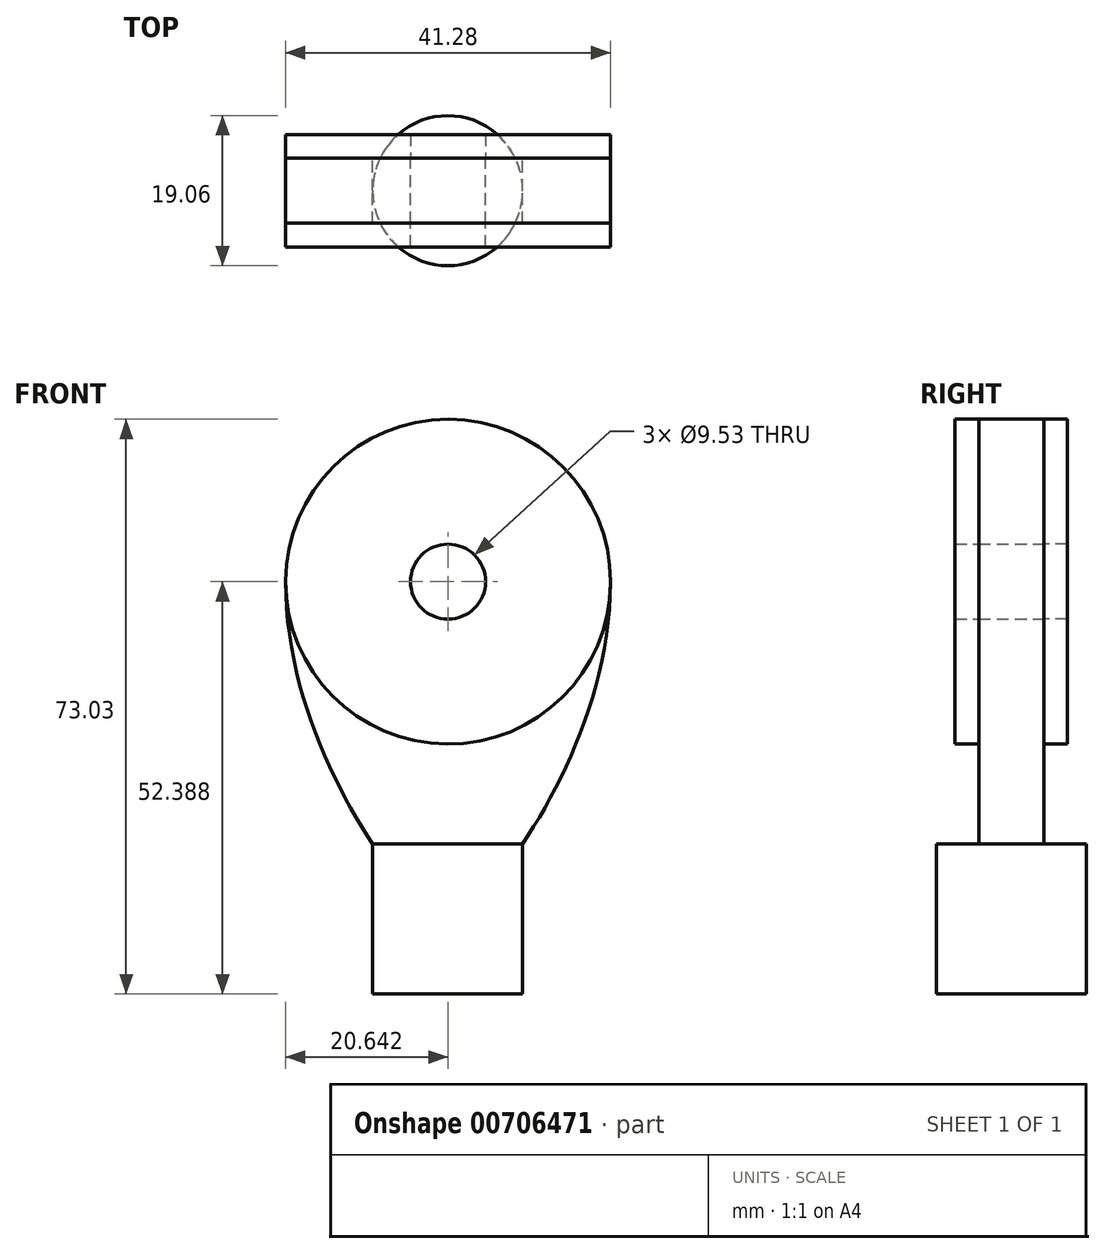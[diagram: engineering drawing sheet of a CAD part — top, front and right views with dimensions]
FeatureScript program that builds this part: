
annotation { "Feature Type Name" : "Feature", "Feature Type Description" : "" }
export const myFeature = defineFeature(function(context is Context, id is Id, definition is map)
    precondition{}
    {
        {
            var Q0;
            Q0=qCreatedBy(makeId("Front.planeOp"),FACE);
            var sketch = newSketch(context, id + "F0", { "sketchPlane" : qUnion([Q0])});
            skCircle(sketch, "E0", {"center": v(0.05, 6.8) * mm, "radius": 20.64 * mm});
            skLineSegment(sketch, "E1.bottom", {"start": v(-9.53, -26.53) * mm, "end": v(9.53, -26.53) * mm});
            skLineSegment(sketch, "E1.top", {"start": v(-9.53, -45.58) * mm, "end": v(9.53, -45.58) * mm});
            skLineSegment(sketch, "E1.left", {"start": v(-9.52, -26.53) * mm, "end": v(-9.52, -45.58) * mm});
            skLineSegment(sketch, "E1.right", {"start": v(9.53, -26.53) * mm, "end": v(9.53, -45.58) * mm});
            skLineSegment(sketch, "E2", {"start": v(0, -26.53) * mm, "end": v(0, -45.58) * mm});
            skPoint(sketch, "E3", {"position": v(-20.59, 6.8) * mm});
            skPoint(sketch, "E4", {"position": v(20.69, 6.8) * mm});
            skFitSpline(sketch, "E5", {"points": [v(-20.59, 6.8) * mm, v(-9.52, -26.53) * mm, v(0, -34.97) * mm, v(9.53, -26.53) * mm, v(20.69, 6.8) * mm], "startDerivative": vector(-0.25, -124.59) * mm, "endDerivative": vector(0.25, 124.63) * mm});
            skLineSegment(sketch, "E6", {"start": v(-20.59, 6.8) * mm, "end": v(20.69, 6.8) * mm, "construction": true});
            skLineSegment(sketch, "E7", {"start": v(-20.61, -6.15) * mm, "end": v(20.66, -6.16) * mm, "construction": true});
            skCircle(sketch, "E8", {"center": v(0.05, 6.8) * mm, "radius": 4.76 * mm});
            skSolve(sketch);
        }
        {
            var Q0;
            {var subQ0=sQuery(id+"F0.wireOp",EDGE,"E1.left");Q0=makeQuery(id+"F0.imprint","IMPRINT",FACE,{"disambiguationData":[TD([[makeQuery(id+"F0.imprint","IMPRINT",EDGE,{"derivedFrom":subQ0}),1.0]])]});}
            var Q1;
            {var subQ1=sQuery(id+"F0.wireOp",EDGE,"E1.bottom");var subQ3=sQuery(id+"F0.wireOp",EDGE,"E2");var subQ4=makeQuery(id+"F0.imprint","INTERSECT",VERTEX,{"derivedFrom":[subQ1,subQ3]});Q1=makeQuery(id+"F0.imprint","IMPRINT",FACE,{"disambiguationData":[TD([[makeQuery(id+"F0.imprint","IMPRINT",EDGE,{"disambiguationData":[TD([[subQ4,-1.0]])],"derivedFrom":subQ3}),-1.0]])]});}
            var Q2;
            Q2=sQuery(id+"F0.wireOp",EDGE,"E2");
            revolve(context, id + "F1", {"surfaceOperationType" : NewSurfaceOperationType.NEW, "entities" : qUnion([Q0, Q1]), "axis" : qUnion([Q2]), "revolveType" : RevolveType.FULL});
        }
        {
            var Q0;
            Q0=makeQuery(id+"F0.imprint","IMPRINT",FACE,{"disambiguationData":[TD([[makeQuery(id+"F0.imprint","IMPRINT",EDGE,{"derivedFrom":sQuery(id+"F0.wireOp",EDGE,"E8")}),-1.0]])]});
            var Q1;
            {var subQ0=sQuery(id+"F0.wireOp",EDGE,"E5");var subQ5=sQuery(id+"F0.wireOp",EDGE,"E0");var subQ7=makeQuery(id+"F0.imprint","INTERSECT",VERTEX,{"disambiguationData":[OD(0.0)],"derivedFrom":[subQ5,subQ0]});Q1=makeQuery(id+"F0.imprint","IMPRINT",FACE,{"disambiguationData":[TD([[makeQuery(id+"F0.imprint","IMPRINT",EDGE,{"disambiguationData":[TD([[subQ7,-1.0]])],"derivedFrom":subQ5}),-1.0]])]});}
            extrude(context, id + "F2", {"entities" : qUnion([Q0, Q1]), "operationType" : NewBodyOperationType.ADD, "depth" : 4.13 * mm, "offsetDistance" : 25.4 * mm, "hasSecondDirection" : true, "secondDirectionOppositeDirection" : true, "secondDirectionDepth" : 4.13 * mm});
        }
        {
            var Q0;
            Q0=makeQuery(id+"F0.imprint","IMPRINT",FACE,{"disambiguationData":[TD([[makeQuery(id+"F0.imprint","IMPRINT",EDGE,{"derivedFrom":sQuery(id+"F0.wireOp",EDGE,"E8")}),-1.0]])]});
            extrude(context, id + "F3", {"entities" : qUnion([Q0]), "depth" : 7.14 * mm, "offsetDistance" : 25.4 * mm, "hasSecondDirection" : true, "secondDirectionOppositeDirection" : true, "secondDirectionDepth" : -4.13 * mm});
        }
        {
            var Q0;
            Q0=makeQuery(id+"F3.opExtrude","SWEPT_BODY",BODY,{"disambiguationData":[OSD([sQuery(id+"F0.wireOp",EDGE,"E0"),sQuery(id+"F0.wireOp",EDGE,"E8")])]});
            var Q1;
            Q1=qCreatedBy(makeId("Front.planeOp"),FACE);
            mirror(context, id + "F4", {"entities" : qUnion([Q0]), "mirrorPlane" : qUnion([Q1])});
        }
    });
